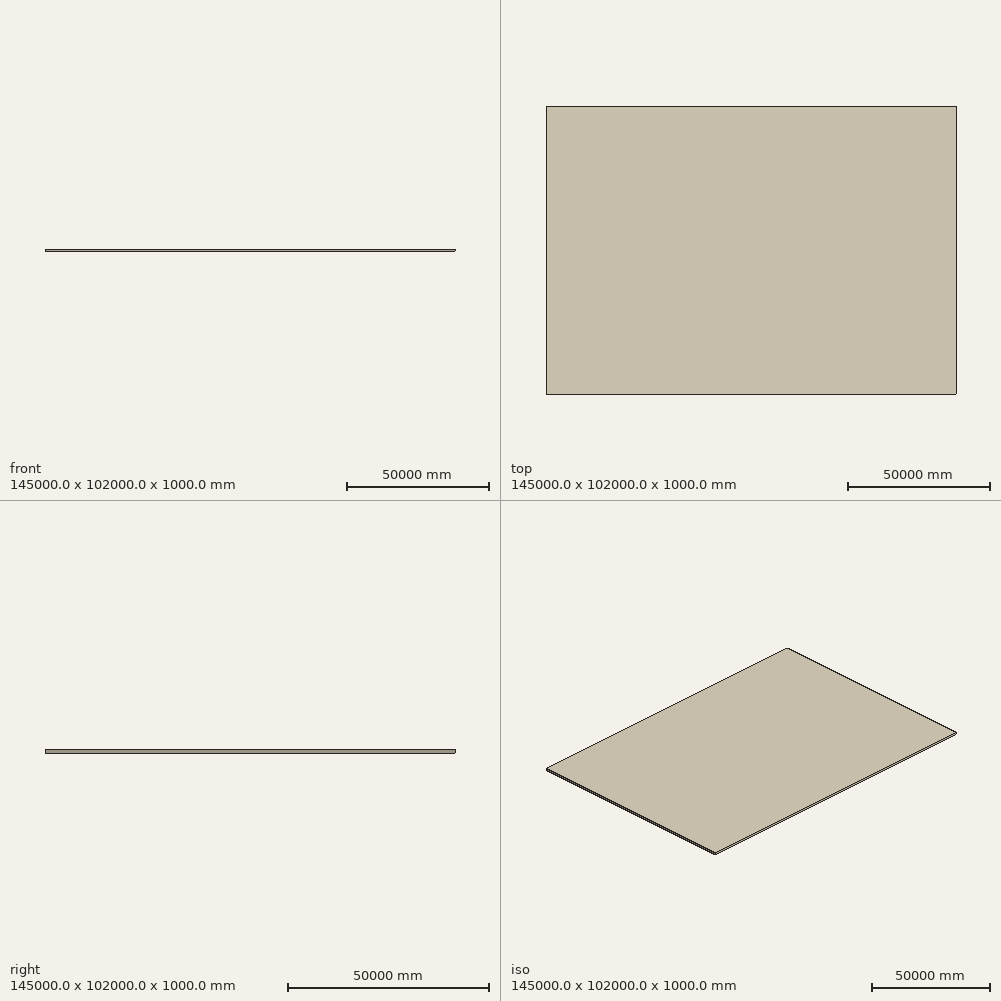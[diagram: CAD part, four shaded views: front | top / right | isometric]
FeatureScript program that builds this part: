
annotation { "Feature Type Name" : "Feature", "Feature Type Description" : "" }
export const myFeature = defineFeature(function(context is Context, id is Id, definition is map)
    precondition{}
    {
        {
            var Q0;
            Q0=qCreatedBy(makeId("Top.planeOp"),FACE);
            var sketch = newSketch(context, id + "F0", { "sketchPlane" : qUnion([Q0])});
            skLineSegment(sketch, "E0", {"start": v(0, 0) * mm, "end": v(-145000, 0) * mm});
            skLineSegment(sketch, "E1", {"start": v(-145000, 0) * mm, "end": v(-145000, 102000) * mm});
            skLineSegment(sketch, "E2", {"start": v(-145000, 102000) * mm, "end": v(0, 102000) * mm});
            skLineSegment(sketch, "E3", {"start": v(0, 102000) * mm, "end": v(0, 0) * mm});
            skSolve(sketch);
        }
        {
            var Q0;
            Q0 = qSketchRegion(id + "F0", true);
            extrude(context, id + "F1", {"entities" : qUnion([Q0]), "depth" : 1000 * mm});
        }
    });
